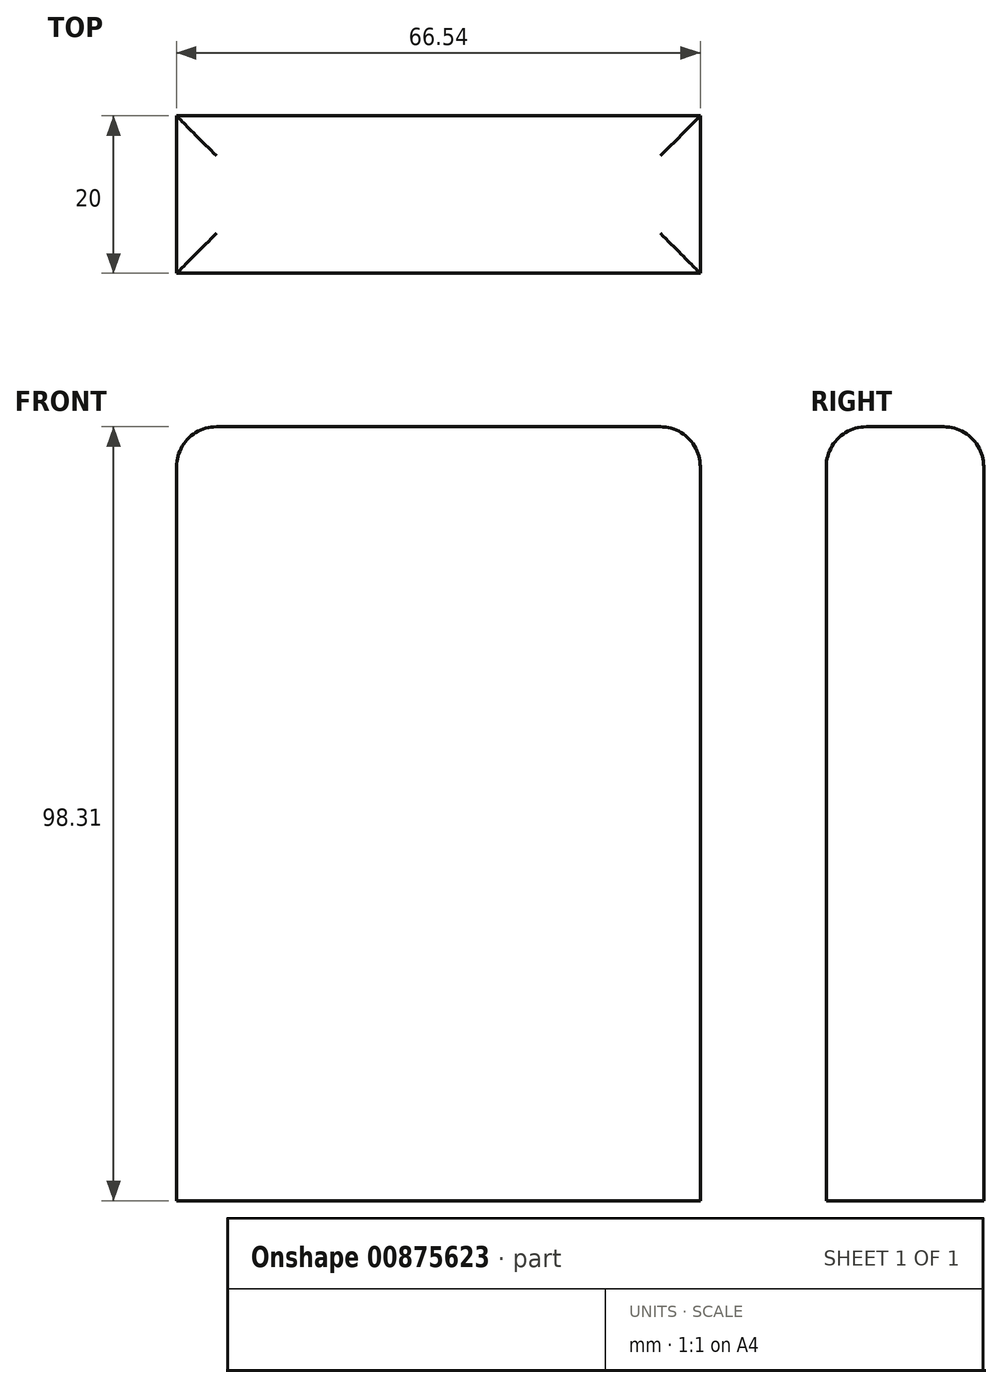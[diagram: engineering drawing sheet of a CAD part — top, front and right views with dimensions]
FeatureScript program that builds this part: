
annotation { "Feature Type Name" : "Feature", "Feature Type Description" : "" }
export const myFeature = defineFeature(function(context is Context, id is Id, definition is map)
    precondition{}
    {
        {
            var Q0;
            Q0=qCreatedBy(makeId("Front.planeOp"),FACE);
            var sketch = newSketch(context, id + "F0", { "sketchPlane" : qUnion([Q0])});
            skLineSegment(sketch, "E0.bottom", {"start": v(33.27, 50.21) * mm, "end": v(-33.27, 50.21) * mm});
            skLineSegment(sketch, "E0.top", {"start": v(33.27, -48.1) * mm, "end": v(-33.27, -48.1) * mm});
            skLineSegment(sketch, "E0.left", {"start": v(33.27, 50.21) * mm, "end": v(33.27, -48.1) * mm});
            skLineSegment(sketch, "E0.right", {"start": v(-33.27, 50.21) * mm, "end": v(-33.27, -48.1) * mm});
            skSolve(sketch);
        }
        {
            var Q0;
            Q0=makeQuery(id+"F0.imprint","IMPRINT",FACE,{"disambiguationData":[TD([[makeQuery(id+"F0.imprint","IMPRINT",EDGE,{"derivedFrom":sQuery(id+"F0.wireOp",EDGE,"E0.bottom")}),1.0]])]});
            extrude(context, id + "F1", {"entities" : qUnion([Q0]), "depth" : 20 * mm, "offsetDistance" : 25.4 * mm});
        }
        {
            var Q0;
            Q0=makeQuery(id+"F1.opExtrude","CAP_FACE",FACE,{"disambiguationData":[OSD([sQuery(id+"F0.wireOp",EDGE,"E0.bottom"),sQuery(id+"F0.wireOp",EDGE,"E0.top"),sQuery(id+"F0.wireOp",EDGE,"E0.left"),sQuery(id+"F0.wireOp",EDGE,"E0.right")])],"isStart":true});
            var sketch = newSketch(context, id + "F2", { "sketchPlane" : qUnion([Q0])});
            skLineSegment(sketch, "E1", {"start": v(-33.27, 0) * mm, "end": v(0, 50.21) * mm});
            skLineSegment(sketch, "E2", {"start": v(0, 50.21) * mm, "end": v(33.27, 0) * mm});
            skSolve(sketch);
        }
        {
            var Q0;
            Q0=makeQuery(id+"F1.opExtrude","CAP_EDGE",EDGE,{"disambiguationData":[OSD([sQuery(id+"F0.wireOp",EDGE,"E0.bottom")])],"isStart":true});
            var Q1;
            Q1=makeQuery(id+"F1.opExtrude","CAP_EDGE",EDGE,{"disambiguationData":[OSD([sQuery(id+"F0.wireOp",EDGE,"E0.bottom")])],"isStart":false});
            var Q2;
            Q2=makeQuery(id+"F1.opExtrude","SWEPT_EDGE",EDGE,{"disambiguationData":[OSD([sQuery(id+"F0.wireOp",EDGE,"E0.bottom"),sQuery(id+"F0.wireOp",EDGE,"E0.left")])]});
            var Q3;
            Q3=makeQuery(id+"F1.opExtrude","SWEPT_EDGE",EDGE,{"disambiguationData":[OSD([sQuery(id+"F0.wireOp",EDGE,"E0.bottom"),sQuery(id+"F0.wireOp",EDGE,"E0.right")])]});
            fillet(context, id + "F3", {"entities" : qUnion([Q0, Q1, Q2, Q3]), "radius" : 5.08 * mm, "tangentPropagation" : true, "allowEdgeOverflow" : false});
        }
    });
